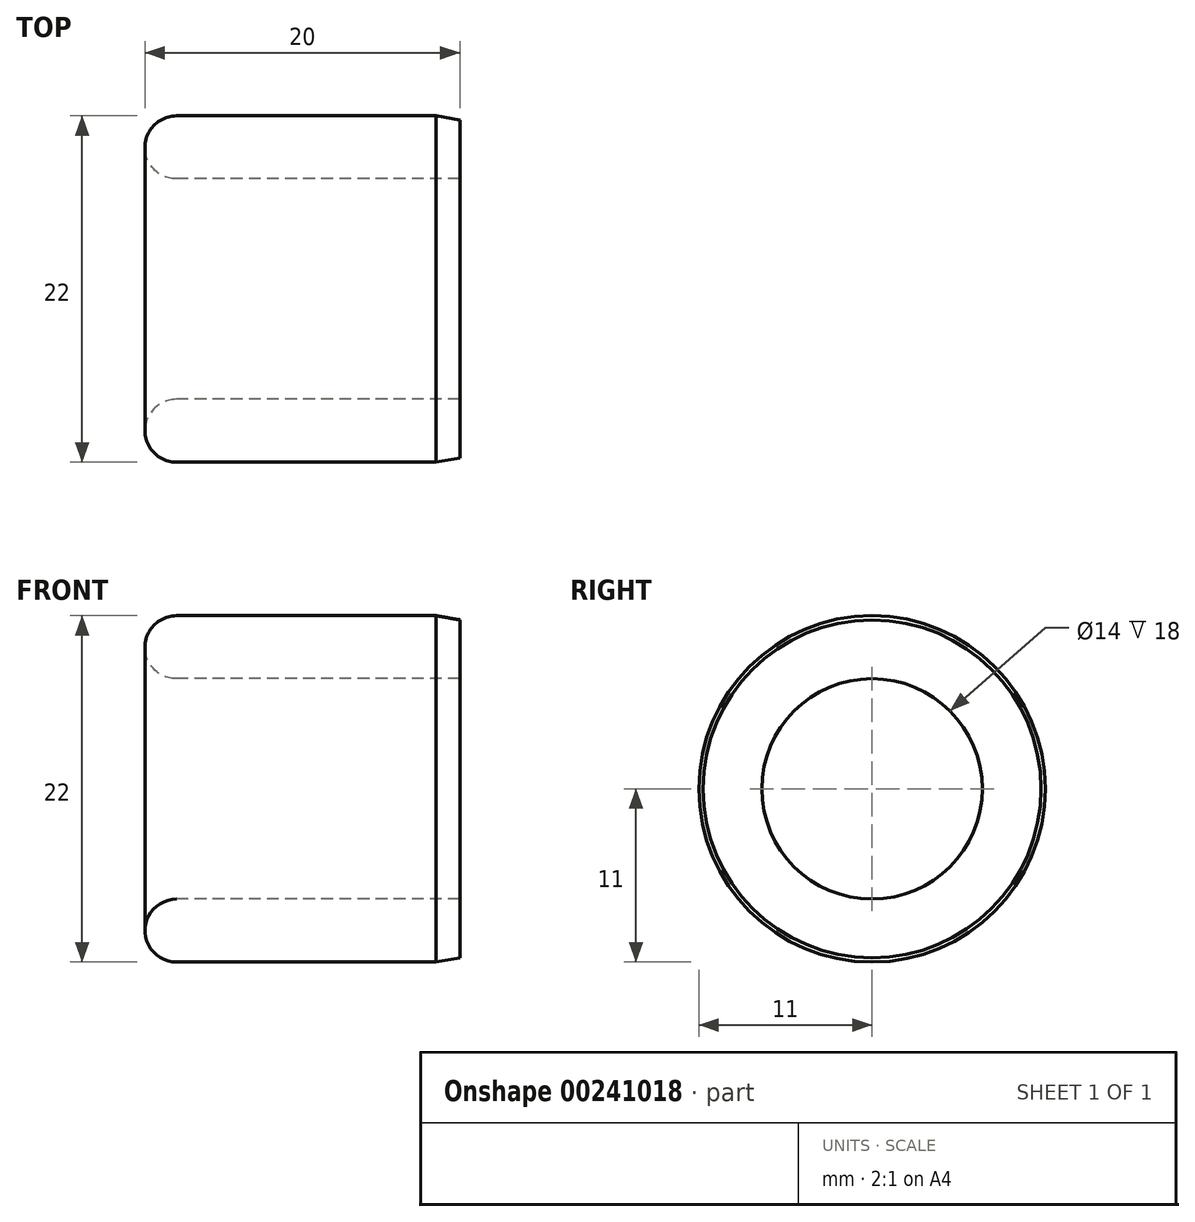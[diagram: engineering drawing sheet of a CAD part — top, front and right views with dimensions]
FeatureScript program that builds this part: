
annotation { "Feature Type Name" : "Feature", "Feature Type Description" : "" }
export const myFeature = defineFeature(function(context is Context, id is Id, definition is map)
    precondition{}
    {
        {
            var Q0;
            Q0=qCreatedBy(makeId("Front.planeOp"),FACE);
            var sketch = newSketch(context, id + "F0", { "sketchPlane" : qUnion([Q0])});
            skLineSegment(sketch, "E0.bottom", {"start": v(0, 11) * mm, "end": v(20, 11) * mm});
            skLineSegment(sketch, "E0.top", {"start": v(0, 7) * mm, "end": v(20, 7) * mm});
            skLineSegment(sketch, "E0.left", {"start": v(0, 11) * mm, "end": v(0, 7) * mm});
            skLineSegment(sketch, "E0.right", {"start": v(20, 11) * mm, "end": v(20, 7) * mm});
            skLineSegment(sketch, "E1", {"start": v(-2.28, 0) * mm, "end": v(27.57, 0) * mm, "construction": true});
            skSolve(sketch);
        }
        {
            var Q0;
            Q0=makeQuery(id+"F0.imprint","IMPRINT",FACE,{"disambiguationData":[TD([[makeQuery(id+"F0.imprint","IMPRINT",EDGE,{"derivedFrom":sQuery(id+"F0.wireOp",EDGE,"E0.bottom")}),-1.0]])]});
            var Q1;
            Q1=sQuery(id+"F0.wireOp",EDGE,"E1");
            revolve(context, id + "F1", {"entities" : qUnion([Q0]), "axis" : qUnion([Q1]), "revolveType" : RevolveType.FULL});
        }
        {
            var Q0;
            Q0=qCreatedBy(makeId("Front.planeOp"),FACE);
            var sketch = newSketch(context, id + "F2", { "sketchPlane" : qUnion([Q0])});
            skLineSegment(sketch, "E2", {"start": v(13, 11.97) * mm, "end": v(24, 10.03) * mm});
            skLineSegment(sketch, "E3", {"start": v(24, 10.03) * mm, "end": v(24, 11.97) * mm});
            skLineSegment(sketch, "E4", {"start": v(24, 11.97) * mm, "end": v(13, 11.97) * mm});
            skPoint(sketch, "E5", {"position": v(18.5, 11) * mm});
            skLineSegment(sketch, "E6", {"start": v(-1.77, 0) * mm, "end": v(24.31, 0) * mm, "construction": true});
            skSolve(sketch);
        }
        {
            var Q0;
            Q0=makeQuery(id+"F2.imprint","IMPRINT",FACE,{"disambiguationData":[TD([[makeQuery(id+"F2.imprint","IMPRINT",EDGE,{"derivedFrom":sQuery(id+"F2.wireOp",EDGE,"E2")}),1.0]])]});
            var Q1;
            Q1=sQuery(id+"F2.wireOp",EDGE,"E6");
            revolve(context, id + "F3", {"operationType" : NewBodyOperationType.REMOVE, "entities" : qUnion([Q0]), "axis" : qUnion([Q1]), "revolveType" : RevolveType.FULL, "oppositeDirection" : true});
        }
        {
            var Q0;
            Q0=makeQuery(id+"F1.opRevolve","SWEPT_EDGE",EDGE,{"disambiguationData":[OSD([sQuery(id+"F0.wireOp",EDGE,"E0.bottom"),sQuery(id+"F0.wireOp",EDGE,"E0.left")])]});
            var Q1;
            Q1=makeQuery(id+"F1.opRevolve","SWEPT_EDGE",EDGE,{"disambiguationData":[OSD([sQuery(id+"F0.wireOp",EDGE,"E0.top"),sQuery(id+"F0.wireOp",EDGE,"E0.left")])]});
            fillet(context, id + "F4", {"entities" : qUnion([Q0, Q1]), "radius" : 2 * mm, "tangentPropagation" : true, "allowEdgeOverflow" : false});
        }
    });
